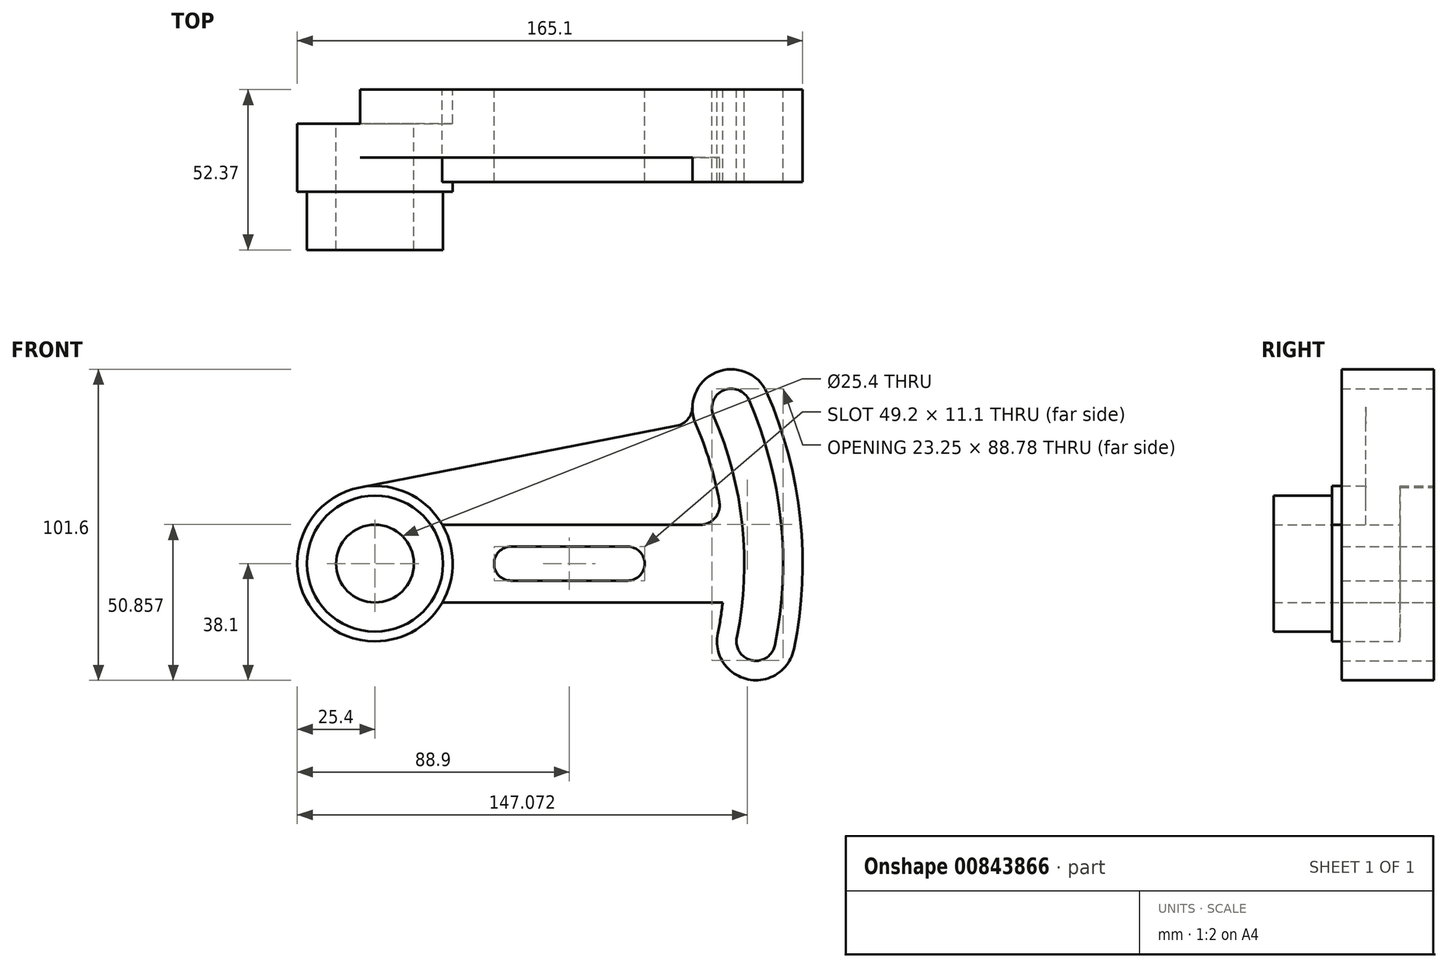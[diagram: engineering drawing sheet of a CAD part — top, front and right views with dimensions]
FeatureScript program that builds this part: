
annotation { "Feature Type Name" : "Feature", "Feature Type Description" : "" }
export const myFeature = defineFeature(function(context is Context, id is Id, definition is map)
    precondition{}
    {
        {
            var Q0;
            Q0=qCreatedBy(makeId("Front.planeOp"),FACE);
            var sketch = newSketch(context, id + "F0", { "sketchPlane" : qUnion([Q0])});
            skCircle(sketch, "E0", {"center": v(0, 0) * mm, "radius": 22.23 * mm});
            skCircle(sketch, "E1", {"center": v(0, 0) * mm, "radius": 25.4 * mm});
            skCircle(sketch, "E2", {"center": v(0, 0) * mm, "radius": 12.7 * mm});
            skArc(sketch, "E3", {"start": v(44.45, 5.55) * mm, "mid": v(38.9, 0) * mm, "end": v(44.45, -5.55) * mm});
            skArc(sketch, "E4", {"start": v(82.55, -5.55) * mm, "mid": v(88.1, 0) * mm, "end": v(82.55, 5.55) * mm});
            skLineSegment(sketch, "E5", {"start": v(44.45, -5.55) * mm, "end": v(82.55, -5.55) * mm});
            skLineSegment(sketch, "E6", {"start": v(82.55, 5.55) * mm, "end": v(44.45, 5.55) * mm});
            skLineSegment(sketch, "E7", {"start": v(44.45, -12.7) * mm, "end": v(22, -12.7) * mm});
            skLineSegment(sketch, "E8", {"start": v(44.45, 12.7) * mm, "end": v(22, 12.7) * mm});
            skLineSegment(sketch, "E9", {"start": v(22.23, 0) * mm, "end": v(38.9, 0) * mm});
            skPoint(sketch, "E9.endSnap0", {"position": v(88.1, 0) * mm});
            skArc(sketch, "E10", {"start": v(118.21, -24.13) * mm, "mid": v(123.16, -31.62) * mm, "end": v(130.66, -26.67) * mm});
            skArc(sketch, "E11", {"start": v(122.22, 53.34) * mm, "mid": v(113.86, 56.62) * mm, "end": v(110.58, 48.26) * mm});
            skArc(sketch, "E12", {"start": v(128.04, 55.88) * mm, "mid": v(111.32, 62.44) * mm, "end": v(104.76, 45.72) * mm});
            skArc(sketch, "E13", {"start": v(112, -22.86) * mm, "mid": v(121.9, -37.84) * mm, "end": v(136.88, -27.94) * mm});
            skLineSegment(sketch, "E14", {"start": v(111.44, -25.4) * mm, "end": v(111.73, -25.4) * mm});
            skArc(sketch, "E15", {"start": v(136.88, -27.94) * mm, "mid": v(138.93, 14.65) * mm, "end": v(128.04, 55.88) * mm});
            skLineSegment(sketch, "E16", {"start": v(44.45, 12.7) * mm, "end": v(106.26, 12.7) * mm});
            skLineSegment(sketch, "E17", {"start": v(44.45, -12.7) * mm, "end": v(113.6, -12.7) * mm});
            skArc(sketch, "E18", {"start": v(118.21, -24.13) * mm, "mid": v(119.98, 12.65) * mm, "end": v(110.58, 48.26) * mm});
            skArc(sketch, "E19", {"start": v(130.66, -26.67) * mm, "mid": v(132.61, 13.99) * mm, "end": v(122.22, 53.34) * mm});
            skPoint(sketch, "E20.orphan", {"position": v(114.3, 0) * mm});
            skLineSegment(sketch, "E21.trimOffspring", {"start": v(22.23, 0) * mm, "end": v(25.4, 0) * mm});
            skLineSegment(sketch, "E22", {"start": v(-4.85, 24.93) * mm, "end": v(98.56, 45.03) * mm});
            skArc(sketch, "E23.filletArc", {"start": v(106.26, 12.7) * mm, "mid": v(111.13, 14.98) * mm, "end": v(112.5, 20.17) * mm});
            skArc(sketch, "E24.filletArc", {"start": v(98.56, 45.03) * mm, "mid": v(102.2, 47.17) * mm, "end": v(103.7, 51.11) * mm});
            skArc(sketch, "E25", {"start": v(111.44, -25.4) * mm, "mid": v(113.8, 10.7) * mm, "end": v(104.76, 45.72) * mm});
            skSolve(sketch);
        }
        {
            var Q0;
            Q0=makeQuery(id+"F0.imprint","IMPRINT",FACE,{"disambiguationData":[TD([[makeQuery(id+"F0.imprint","IMPRINT",EDGE,{"derivedFrom":sQuery(id+"F0.wireOp",EDGE,"E0")}),-1.0]])]});
            var Q1;
            Q1=makeQuery(id+"F0.imprint","IMPRINT",FACE,{"disambiguationData":[TD([[makeQuery(id+"F0.imprint","IMPRINT",EDGE,{"derivedFrom":sQuery(id+"F0.wireOp",EDGE,"E4")}),-1.0]])]});
            var Q2;
            Q2=makeQuery(id+"F0.imprint","IMPRINT",FACE,{"disambiguationData":[TD([[makeQuery(id+"F0.imprint","IMPRINT",EDGE,{"derivedFrom":sQuery(id+"F0.wireOp",EDGE,"E10")}),-1.0]])]});
            extrude(context, id + "F1", {"entities" : qUnion([Q0, Q1, Q2]), "depth" : 33.32 * mm, "offsetDistance" : 25.4 * mm});
        }
        {
            var Q0;
            Q0=makeQuery(id+"F0.imprint","IMPRINT",FACE,{"disambiguationData":[TD([[makeQuery(id+"F0.imprint","IMPRINT",EDGE,{"derivedFrom":sQuery(id+"F0.wireOp",EDGE,"E0")}),1.0]])]});
            extrude(context, id + "F2", {"entities" : qUnion([Q0]), "operationType" : NewBodyOperationType.ADD, "depth" : 52.37 * mm, "offsetDistance" : 25.4 * mm});
        }
        {
            var Q0;
            Q0=makeQuery(id+"F1.opExtrude","CAP_FACE",FACE,{"disambiguationData":[OSD([sQuery(id+"F0.wireOp",EDGE,"E0"),sQuery(id+"F0.wireOp",EDGE,"E1"),sQuery(id+"F0.wireOp",EDGE,"E3"),sQuery(id+"F0.wireOp",EDGE,"E4"),sQuery(id+"F0.wireOp",EDGE,"E5"),sQuery(id+"F0.wireOp",EDGE,"E6"),sQuery(id+"F0.wireOp",EDGE,"E7"),sQuery(id+"F0.wireOp",EDGE,"E8"),sQuery(id+"F0.wireOp",EDGE,"E10"),sQuery(id+"F0.wireOp",EDGE,"E11"),sQuery(id+"F0.wireOp",EDGE,"E12"),sQuery(id+"F0.wireOp",EDGE,"E13"),sQuery(id+"F0.wireOp",EDGE,"E15"),sQuery(id+"F0.wireOp",EDGE,"E16"),sQuery(id+"F0.wireOp",EDGE,"E17"),sQuery(id+"F0.wireOp",EDGE,"E18"),sQuery(id+"F0.wireOp",EDGE,"E19"),sQuery(id+"F0.wireOp",EDGE,"E23.filletArc"),sQuery(id+"F0.wireOp",EDGE,"E24.filletArc"),sQuery(id+"F0.wireOp",EDGE,"E25")])],"isStart":false});
            var sketch = newSketch(context, id + "F3", { "sketchPlane" : qUnion([Q0])});
            skCircle(sketch, "E26", {"center": v(0, 0) * mm, "radius": 25.4 * mm});
            skSolve(sketch);
        }
        {
            var Q0;
            Q0=makeQuery(id+"F3.imprint","IMPRINT",FACE,{"disambiguationData":[TD([[makeQuery(id+"F3.imprint","IMPRINT",EDGE,{"derivedFrom":makeQuery(id+"F1.opExtrude","CAP_EDGE",EDGE,{"disambiguationData":[OSD([sQuery(id+"F0.wireOp",EDGE,"E3")])],"isStart":false})}),-1.0]])]});
            extrude(context, id + "F4", {"entities" : qUnion([Q0]), "operationType" : NewBodyOperationType.REMOVE, "oppositeDirection" : true, "depth" : 3.17 * mm, "offsetDistance" : 25.4 * mm});
        }
        {
            var Q0;
            {var subQ0=sQuery(id+"F0.wireOp",EDGE,"E0");Q0=makeQuery(id+"F2.boolean.opBoolean","MERGE",FACE,{"derivedFrom":[makeQuery(id+"F1.opExtrude","CAP_FACE",FACE,{"disambiguationData":[OSD([subQ0,sQuery(id+"F0.wireOp",EDGE,"E1"),sQuery(id+"F0.wireOp",EDGE,"E3"),sQuery(id+"F0.wireOp",EDGE,"E4"),sQuery(id+"F0.wireOp",EDGE,"E5"),sQuery(id+"F0.wireOp",EDGE,"E6"),sQuery(id+"F0.wireOp",EDGE,"E7"),sQuery(id+"F0.wireOp",EDGE,"E8"),sQuery(id+"F0.wireOp",EDGE,"E10"),sQuery(id+"F0.wireOp",EDGE,"E11"),sQuery(id+"F0.wireOp",EDGE,"E12"),sQuery(id+"F0.wireOp",EDGE,"E13"),sQuery(id+"F0.wireOp",EDGE,"E15"),sQuery(id+"F0.wireOp",EDGE,"E16"),sQuery(id+"F0.wireOp",EDGE,"E17"),sQuery(id+"F0.wireOp",EDGE,"E18"),sQuery(id+"F0.wireOp",EDGE,"E19"),sQuery(id+"F0.wireOp",EDGE,"E23.filletArc"),sQuery(id+"F0.wireOp",EDGE,"E24.filletArc"),sQuery(id+"F0.wireOp",EDGE,"E25")])],"isStart":true}),makeQuery(id+"F2.opExtrude","CAP_FACE",FACE,{"disambiguationData":[OSD([subQ0,sQuery(id+"F0.wireOp",EDGE,"E2")])],"isStart":true})]});}
            var sketch = newSketch(context, id + "F5", { "sketchPlane" : qUnion([Q0])});
            skCircle(sketch, "E27", {"center": v(0, 0) * mm, "radius": 25.4 * mm});
            skSolve(sketch);
        }
        {
            var Q0;
            Q0=makeQuery(id+"F5.imprint","IMPRINT",FACE,{"disambiguationData":[TD([[makeQuery(id+"F5.imprint","IMPRINT",EDGE,{"disambiguationData":[OD(1.0)],"derivedFrom":sQuery(id+"F5.wireOp",EDGE,"E27")}),-1.0]])]});
            extrude(context, id + "F6", {"entities" : qUnion([Q0]), "operationType" : NewBodyOperationType.REMOVE, "oppositeDirection" : true, "depth" : 3.17 * mm, "offsetDistance" : 25.4 * mm});
        }
        {
            var Q0;
            {var subQ1=sQuery(id+"F0.wireOp",EDGE,"E8");Q0=makeQuery(id+"F0.imprint","IMPRINT",FACE,{"disambiguationData":[TD([[makeQuery(id+"F0.imprint","IMPRINT",EDGE,{"derivedFrom":subQ1}),-1.0]])]});}
            extrude(context, id + "F7", {"entities" : qUnion([Q0]), "operationType" : NewBodyOperationType.ADD, "depth" : 22.22 * mm, "offsetDistance" : 25.4 * mm});
        }
        {
            var Q0;
            {var subQ0=sQuery(id+"F0.wireOp",EDGE,"E25");var subQ1=sQuery(id+"F0.wireOp",EDGE,"E24.filletArc");var subQ2=sQuery(id+"F0.wireOp",EDGE,"E23.filletArc");var subQ3=sQuery(id+"F0.wireOp",EDGE,"E16");var subQ4=sQuery(id+"F0.wireOp",EDGE,"E8");var subQ5=sQuery(id+"F0.wireOp",EDGE,"E1");var subQ6=sQuery(id+"F0.wireOp",EDGE,"E0");Q0=makeQuery(id+"F7.boolean.opBoolean","MERGE",FACE,{"derivedFrom":[makeQuery(id+"F2.boolean.opBoolean","MERGE",FACE,{"derivedFrom":[makeQuery(id+"F1.opExtrude","CAP_FACE",FACE,{"disambiguationData":[OSD([subQ6,subQ5,sQuery(id+"F0.wireOp",EDGE,"E3"),sQuery(id+"F0.wireOp",EDGE,"E4"),sQuery(id+"F0.wireOp",EDGE,"E5"),sQuery(id+"F0.wireOp",EDGE,"E6"),sQuery(id+"F0.wireOp",EDGE,"E7"),subQ4,sQuery(id+"F0.wireOp",EDGE,"E10"),sQuery(id+"F0.wireOp",EDGE,"E11"),sQuery(id+"F0.wireOp",EDGE,"E12"),sQuery(id+"F0.wireOp",EDGE,"E13"),sQuery(id+"F0.wireOp",EDGE,"E15"),subQ3,sQuery(id+"F0.wireOp",EDGE,"E17"),sQuery(id+"F0.wireOp",EDGE,"E18"),sQuery(id+"F0.wireOp",EDGE,"E19"),subQ2,subQ1,subQ0])],"isStart":true}),makeQuery(id+"F2.opExtrude","CAP_FACE",FACE,{"disambiguationData":[OSD([subQ6,sQuery(id+"F0.wireOp",EDGE,"E2")])],"isStart":true})]}),makeQuery(id+"F7.opExtrude","CAP_FACE",FACE,{"disambiguationData":[OSD([subQ5,subQ4,subQ3,sQuery(id+"F0.wireOp",EDGE,"E22"),subQ2,subQ1,subQ0])],"isStart":true})]});}
            var sketch = newSketch(context, id + "F8", { "sketchPlane" : qUnion([Q0])});
            skCircle(sketch, "E28", {"center": v(0, 0) * mm, "radius": 25.4 * mm});
            skSolve(sketch);
        }
        {
            var Q0;
            Q0=makeQuery(id+"F8.imprint","IMPRINT",FACE,{"disambiguationData":[TD([[makeQuery(id+"F8.imprint","IMPRINT",EDGE,{"disambiguationData":[OD(0.0)],"derivedFrom":sQuery(id+"F8.wireOp",EDGE,"E28")}),-1.0]])]});
            extrude(context, id + "F9", {"entities" : qUnion([Q0]), "operationType" : NewBodyOperationType.REMOVE, "oppositeDirection" : true, "depth" : 11.1 * mm, "offsetDistance" : 25.4 * mm});
        }
    });
